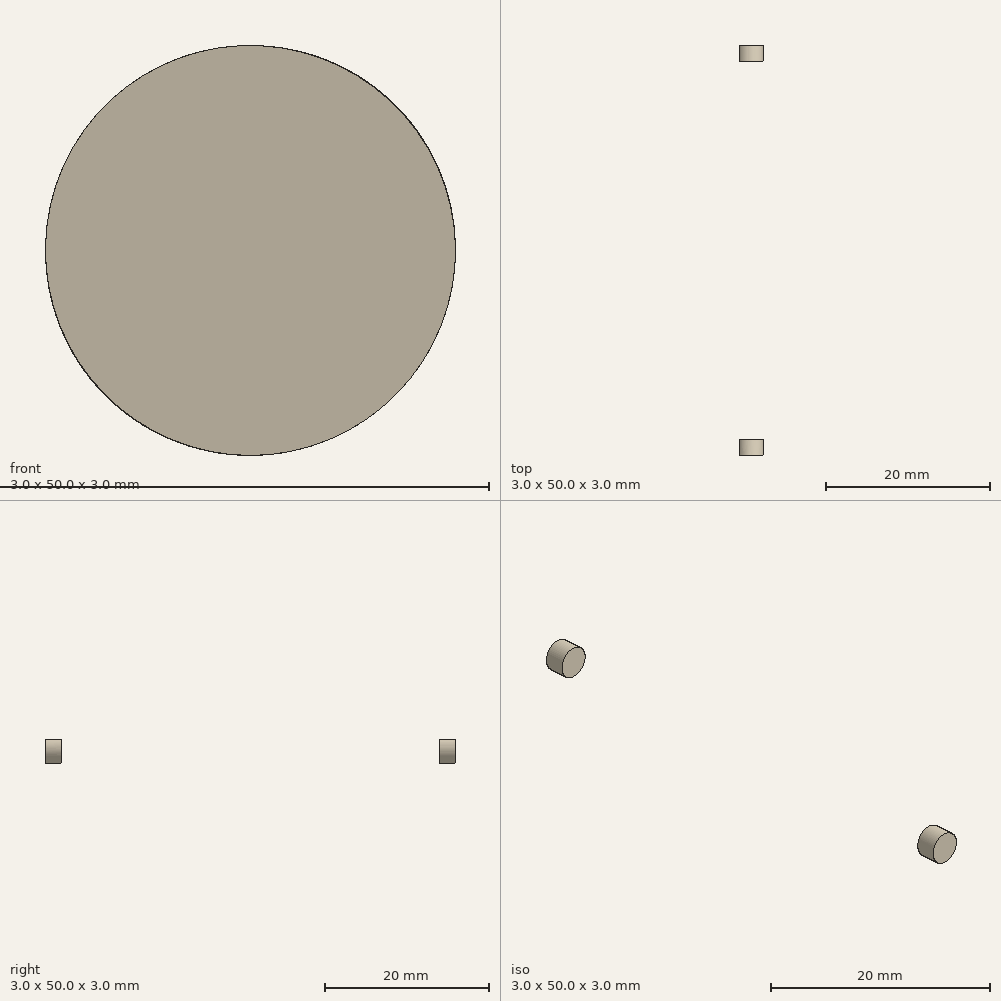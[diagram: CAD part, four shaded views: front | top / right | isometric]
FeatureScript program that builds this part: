
annotation { "Feature Type Name" : "Feature", "Feature Type Description" : "" }
export const myFeature = defineFeature(function(context is Context, id is Id, definition is map)
    precondition{}
    {
        {
            var Q0;
            Q0=qCreatedBy(makeId("Top.planeOp"),FACE);
            var sketch = newSketch(context, id + "F0", { "sketchPlane" : qUnion([Q0])});
            skLineSegment(sketch, "E0.bottom", {"start": v(38, 23) * mm, "end": v(-38, 23) * mm});
            skLineSegment(sketch, "E0.top", {"start": v(38, -23) * mm, "end": v(-38, -23) * mm});
            skLineSegment(sketch, "E0.left", {"start": v(38, 23) * mm, "end": v(38, -23) * mm});
            skLineSegment(sketch, "E0.right", {"start": v(-38, 23) * mm, "end": v(-38, -23) * mm});
            skPoint(sketch, "E0.middle", {"position": v(0, 0) * mm});
            skLineSegment(sketch, "E1.bottom", {"start": v(40, 25) * mm, "end": v(-40, 25) * mm});
            skLineSegment(sketch, "E1.top", {"start": v(40, -25) * mm, "end": v(-40, -25) * mm});
            skLineSegment(sketch, "E1.left", {"start": v(40, 25) * mm, "end": v(40, -25) * mm});
            skLineSegment(sketch, "E1.right", {"start": v(-40, 25) * mm, "end": v(-40, -25) * mm});
            skSolve(sketch);
        }
        {
            var Q0;
            Q0=makeQuery(id+"F0.imprint","IMPRINT",FACE,{"disambiguationData":[TD([[makeQuery(id+"F0.imprint","IMPRINT",EDGE,{"derivedFrom":sQuery(id+"F0.wireOp",EDGE,"E0.bottom")}),-1.0]])]});
            extrude(context, id + "F1", {"entities" : qUnion([Q0]), "endBound" : BoundingType.SYMMETRIC, "oppositeDirection" : true, "depth" : 10 * mm, "offsetDistance" : 25.4 * mm});
        }
        {
            var Q0;
            Q0=makeQuery(id+"F1.opExtrude","SWEPT_FACE",FACE,{"disambiguationData":[OSD([sQuery(id+"F0.wireOp",EDGE,"E1.top")])]});
            var sketch = newSketch(context, id + "F2", { "sketchPlane" : qUnion([Q0])});
            skCircle(sketch, "E2", {"center": v(0, 0) * mm, "radius": 1.5 * mm});
            skCircle(sketch, "E3", {"center": v(27.32, 0) * mm, "radius": 1.5 * mm});
            skCircle(sketch, "E4.MirrorC", {"center": v(-27.32, 0) * mm, "radius": 1.5 * mm});
            skSolve(sketch);
        }
        {
            var Q0;
            Q0=makeQuery(id+"F2.imprint","IMPRINT",FACE,{"disambiguationData":[TD([[makeQuery(id+"F2.imprint","IMPRINT",EDGE,{"derivedFrom":sQuery(id+"F2.wireOp",EDGE,"E4.MirrorC")}),-1.0]])]});
            var Q1;
            Q1=makeQuery(id+"F2.imprint","IMPRINT",FACE,{"disambiguationData":[TD([[makeQuery(id+"F2.imprint","IMPRINT",EDGE,{"derivedFrom":sQuery(id+"F2.wireOp",EDGE,"E2")}),1.0]])]});
            var Q2;
            Q2=makeQuery(id+"F2.imprint","IMPRINT",FACE,{"disambiguationData":[TD([[makeQuery(id+"F2.imprint","IMPRINT",EDGE,{"derivedFrom":sQuery(id+"F2.wireOp",EDGE,"E3")}),1.0]])]});
            extrude(context, id + "F3", {"entities" : qUnion([Q0, Q1, Q2]), "operationType" : NewBodyOperationType.REMOVE, "endBound" : BoundingType.THROUGH_ALL, "oppositeDirection" : true, "depth" : 25.4 * mm, "offsetDistance" : 25.4 * mm});
        }
    });
